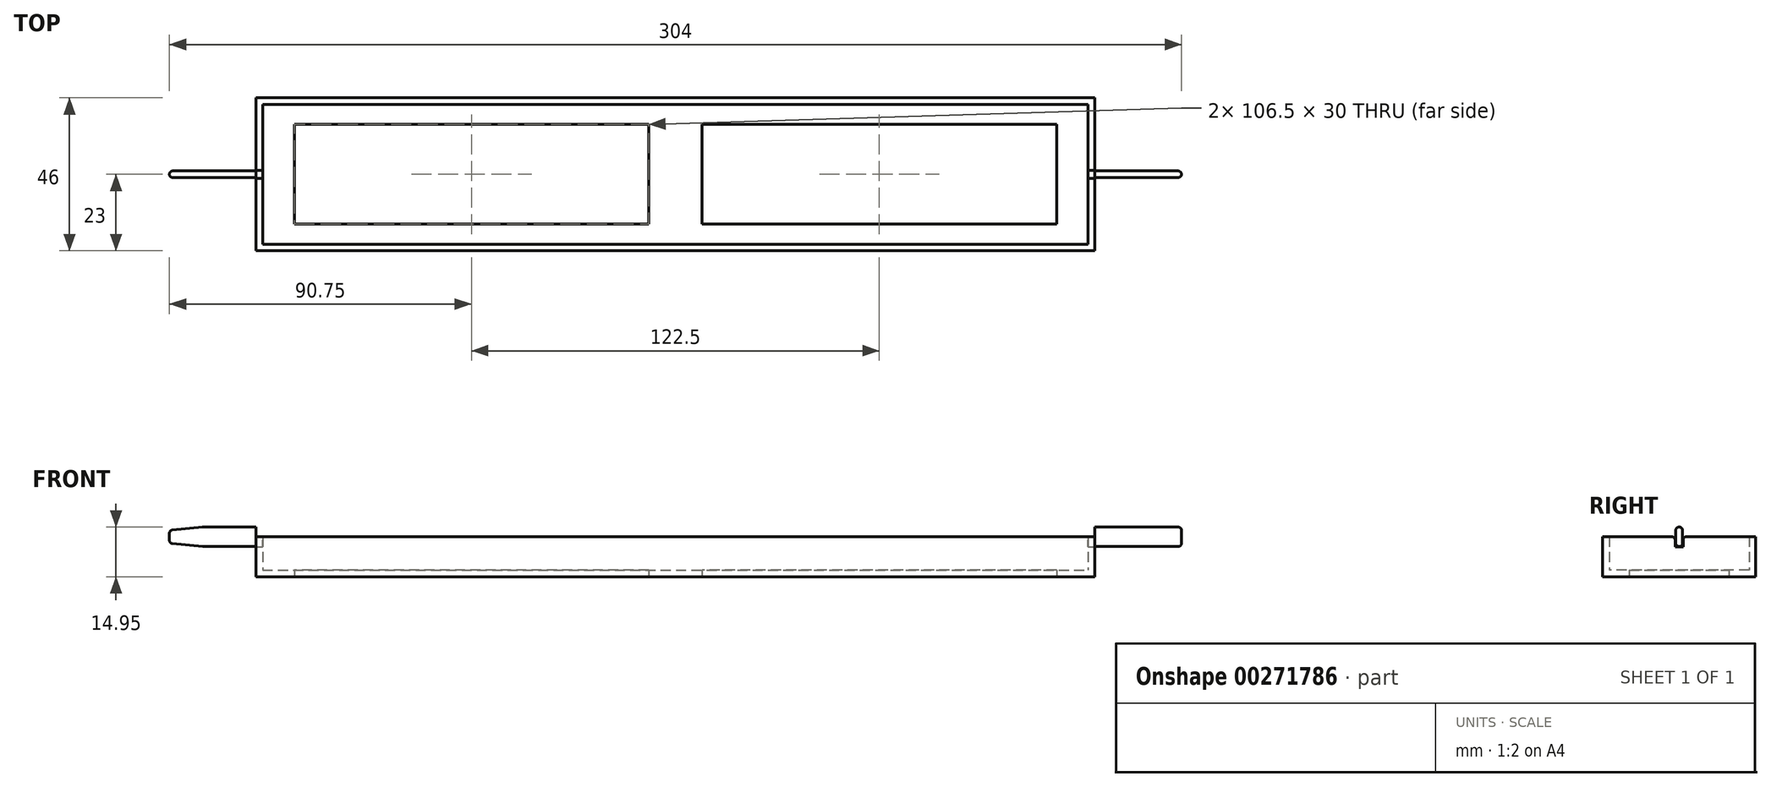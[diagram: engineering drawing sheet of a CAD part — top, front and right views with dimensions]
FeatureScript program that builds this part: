
annotation { "Feature Type Name" : "Feature", "Feature Type Description" : "" }
export const myFeature = defineFeature(function(context is Context, id is Id, definition is map)
    precondition{}
    {
        {
            var Q0;
            Q0=qCreatedBy(makeId("Top.planeOp"),FACE);
            var sketch = newSketch(context, id + "F0", { "sketchPlane" : qUnion([Q0])});
            skLineSegment(sketch, "E0.bottom", {"start": v(126, 23) * mm, "end": v(-126, 23) * mm});
            skLineSegment(sketch, "E0.top", {"start": v(126, -23) * mm, "end": v(-126, -23) * mm});
            skLineSegment(sketch, "E0.left", {"start": v(126, 23) * mm, "end": v(126, -23) * mm});
            skLineSegment(sketch, "E0.right", {"start": v(-126, 23) * mm, "end": v(-126, -23) * mm});
            skPoint(sketch, "E0.middle", {"position": v(0, 0) * mm});
            skLineSegment(sketch, "E1.bottom", {"start": v(114.5, -15) * mm, "end": v(8, -15) * mm});
            skLineSegment(sketch, "E1.top", {"start": v(114.5, 15) * mm, "end": v(8, 15) * mm});
            skLineSegment(sketch, "E1.left", {"start": v(114.5, -15) * mm, "end": v(114.5, 15) * mm});
            skLineSegment(sketch, "E1.right", {"start": v(-114.5, -15) * mm, "end": v(-114.5, 15) * mm});
            skLineSegment(sketch, "E2.left", {"start": v(8, -15) * mm, "end": v(8, 15) * mm});
            skLineSegment(sketch, "E2.right", {"start": v(-8, -15) * mm, "end": v(-8, 15) * mm});
            skLineSegment(sketch, "E3.trimOffspring", {"start": v(-8, 15) * mm, "end": v(-114.5, 15) * mm});
            skLineSegment(sketch, "E4.trimOffspring", {"start": v(-8, -15) * mm, "end": v(-114.5, -15) * mm});
            skSolve(sketch);
        }
        {
            var Q0;
            Q0 = qSketchRegion(id + "F0", true);
            extrude(context, id + "F1", {"entities" : qUnion([Q0]), "depth" : 2 * mm});
        }
        {
            var Q0;
            Q0=makeQuery(id+"F1.opExtrude","CAP_FACE",FACE,{"disambiguationData":[OSD([sQuery(id+"F0.wireOp",EDGE,"E0.bottom"),sQuery(id+"F0.wireOp",EDGE,"E0.top"),sQuery(id+"F0.wireOp",EDGE,"E0.left"),sQuery(id+"F0.wireOp",EDGE,"E0.right")])],"isStart":false});
            var sketch = newSketch(context, id + "F2", { "sketchPlane" : qUnion([Q0])});
            skLineSegment(sketch, "E5.bottom", {"start": v(-126, 23) * mm, "end": v(126, 23) * mm});
            skLineSegment(sketch, "E5.top", {"start": v(-126, -23) * mm, "end": v(126, -23) * mm});
            skLineSegment(sketch, "E5.left", {"start": v(-126, 23) * mm, "end": v(-126, -23) * mm});
            skLineSegment(sketch, "E5.right", {"start": v(126, 23) * mm, "end": v(126, -23) * mm});
            skPoint(sketch, "E5.middle", {"position": v(0, 0) * mm});
            skLineSegment(sketch, "E6.bottom", {"start": v(-124, 21) * mm, "end": v(124, 21) * mm});
            skLineSegment(sketch, "E6.top", {"start": v(-124, -21) * mm, "end": v(124, -21) * mm});
            skLineSegment(sketch, "E6.left", {"start": v(-124, 21) * mm, "end": v(-124, -21) * mm});
            skLineSegment(sketch, "E6.right", {"start": v(124, 21) * mm, "end": v(124, -21) * mm});
            skSolve(sketch);
        }
        {
            var Q0;
            Q0 = qSketchRegion(id + "F2", true);
            extrude(context, id + "F3", {"entities" : qUnion([Q0]), "operationType" : NewBodyOperationType.ADD, "depth" : 10 * mm});
        }
        {
            var Q0;
            Q0=qCreatedBy(makeId("Right.planeOp"),FACE);
            var sketch = newSketch(context, id + "F4", { "sketchPlane" : qUnion([Q0])});
            skLineSegment(sketch, "E7.bottom", {"start": v(-1, 9.05) * mm, "end": v(1, 9.05) * mm});
            skLineSegment(sketch, "E7.top", {"start": v(-1, 14.95) * mm, "end": v(1, 14.95) * mm});
            skLineSegment(sketch, "E7.left", {"start": v(-1, 9.05) * mm, "end": v(-1, 14.95) * mm});
            skLineSegment(sketch, "E7.right", {"start": v(1, 9.05) * mm, "end": v(1, 14.95) * mm});
            skPoint(sketch, "E7.middle", {"position": v(0, 12) * mm});
            skSolve(sketch);
        }
        {
            var Q0;
            Q0 = qSketchRegion(id + "F4", true);
            extrude(context, id + "F5", {"entities" : qUnion([Q0]), "depth" : 152 * mm, "hasSecondDirection" : true, "secondDirectionOppositeDirection" : true, "secondDirectionDepth" : 152 * mm});
        }
        {
            var Q0;
            Q0=makeQuery(id+"F5.opExtrude","CAP_EDGE",EDGE,{"disambiguationData":[OSD([sQuery(id+"F4.wireOp",EDGE,"E7.top")])],"isStart":true});
            var Q1;
            Q1=makeQuery(id+"F5.opExtrude","CAP_EDGE",EDGE,{"disambiguationData":[OSD([sQuery(id+"F4.wireOp",EDGE,"E7.bottom")])],"isStart":true});
            chamfer(context, id + "F6", {"entities" : qUnion([Q0, Q1]), "chamferType" : ChamferType.TWO_OFFSETS, "width1" : 1 * mm, "oppositeDirection" : false, "width2" : 10 * mm, "tangentPropagation" : true});
        }
        {
            var Q0;
            Q0=makeQuery(id+"F5.opExtrude","SWEPT_EDGE",EDGE,{"disambiguationData":[OSD([sQuery(id+"F4.wireOp",EDGE,"E7.top"),sQuery(id+"F4.wireOp",EDGE,"E7.left")])]});
            var Q1;
            Q1=makeQuery(id+"F5.opExtrude","SWEPT_EDGE",EDGE,{"disambiguationData":[OSD([sQuery(id+"F4.wireOp",EDGE,"E7.top"),sQuery(id+"F4.wireOp",EDGE,"E7.right")])]});
            var Q2;
            Q2=makeQuery(id+"F5.opExtrude","SWEPT_EDGE",EDGE,{"disambiguationData":[OSD([sQuery(id+"F4.wireOp",EDGE,"E7.bottom"),sQuery(id+"F4.wireOp",EDGE,"E7.left")])]});
            var Q3;
            Q3=makeQuery(id+"F5.opExtrude","SWEPT_EDGE",EDGE,{"disambiguationData":[OSD([sQuery(id+"F4.wireOp",EDGE,"E7.bottom"),sQuery(id+"F4.wireOp",EDGE,"E7.right")])]});
            var Q4;
            Q4=makeQuery(id+"F5.opExtrude","CAP_FACE",FACE,{"disambiguationData":[OSD([sQuery(id+"F4.wireOp",EDGE,"E7.bottom"),sQuery(id+"F4.wireOp",EDGE,"E7.top"),sQuery(id+"F4.wireOp",EDGE,"E7.left"),sQuery(id+"F4.wireOp",EDGE,"E7.right")])],"isStart":true});
            var Q5;
            Q5=makeQuery(id+"F5.opExtrude","CAP_FACE",FACE,{"disambiguationData":[OSD([sQuery(id+"F4.wireOp",EDGE,"E7.bottom"),sQuery(id+"F4.wireOp",EDGE,"E7.top"),sQuery(id+"F4.wireOp",EDGE,"E7.left"),sQuery(id+"F4.wireOp",EDGE,"E7.right")])],"isStart":false});
            var Q6;
            Q6=makeQuery(id+"F6.opChamfer","BLEND_EDGE",EDGE,{"blendedFrom":[makeQuery(id+"F5.opExtrude","CAP_EDGE",EDGE,{"disambiguationData":[OSD([sQuery(id+"F4.wireOp",EDGE,"E7.top")])],"isStart":true}),makeQuery(id+"F5.opExtrude","SWEPT_FACE",FACE,{"disambiguationData":[OSD([sQuery(id+"F4.wireOp",EDGE,"E7.right")])]})],"blendedInto":[makeQuery(id+"F5.opExtrude","SWEPT_FACE",FACE,{"disambiguationData":[OSD([sQuery(id+"F4.wireOp",EDGE,"E7.right")])]})]});
            var Q7;
            Q7=makeQuery(id+"F6.opChamfer","BLEND_EDGE",EDGE,{"blendedFrom":[makeQuery(id+"F5.opExtrude","CAP_EDGE",EDGE,{"disambiguationData":[OSD([sQuery(id+"F4.wireOp",EDGE,"E7.top")])],"isStart":true}),makeQuery(id+"F5.opExtrude","SWEPT_FACE",FACE,{"disambiguationData":[OSD([sQuery(id+"F4.wireOp",EDGE,"E7.left")])]})],"blendedInto":[makeQuery(id+"F5.opExtrude","SWEPT_FACE",FACE,{"disambiguationData":[OSD([sQuery(id+"F4.wireOp",EDGE,"E7.left")])]})]});
            var Q8;
            Q8=makeQuery(id+"F6.opChamfer","BLEND_EDGE",EDGE,{"blendedFrom":[makeQuery(id+"F5.opExtrude","CAP_EDGE",EDGE,{"disambiguationData":[OSD([sQuery(id+"F4.wireOp",EDGE,"E7.bottom")])],"isStart":true}),makeQuery(id+"F5.opExtrude","SWEPT_FACE",FACE,{"disambiguationData":[OSD([sQuery(id+"F4.wireOp",EDGE,"E7.right")])]})],"blendedInto":[makeQuery(id+"F5.opExtrude","SWEPT_FACE",FACE,{"disambiguationData":[OSD([sQuery(id+"F4.wireOp",EDGE,"E7.right")])]})]});
            var Q9;
            Q9=makeQuery(id+"F6.opChamfer","BLEND_EDGE",EDGE,{"blendedFrom":[makeQuery(id+"F5.opExtrude","CAP_EDGE",EDGE,{"disambiguationData":[OSD([sQuery(id+"F4.wireOp",EDGE,"E7.bottom")])],"isStart":true}),makeQuery(id+"F5.opExtrude","SWEPT_FACE",FACE,{"disambiguationData":[OSD([sQuery(id+"F4.wireOp",EDGE,"E7.left")])]})],"blendedInto":[makeQuery(id+"F5.opExtrude","SWEPT_FACE",FACE,{"disambiguationData":[OSD([sQuery(id+"F4.wireOp",EDGE,"E7.left")])]})]});
            var Q10;
            {var subQ0=sQuery(id+"F4.wireOp",EDGE,"E7.top");Q10=makeQuery(id+"F6.opChamfer","BLEND_EDGE",EDGE,{"blendedFrom":[makeQuery(id+"F5.opExtrude","CAP_EDGE",EDGE,{"disambiguationData":[OSD([subQ0])],"isStart":true}),makeQuery(id+"F5.opExtrude","SWEPT_FACE",FACE,{"disambiguationData":[OSD([subQ0])]})],"blendedInto":[makeQuery(id+"F5.opExtrude","SWEPT_FACE",FACE,{"disambiguationData":[OSD([subQ0])]})]});}
            var Q11;
            {var subQ0=sQuery(id+"F4.wireOp",EDGE,"E7.bottom");Q11=makeQuery(id+"F6.opChamfer","BLEND_EDGE",EDGE,{"blendedFrom":[makeQuery(id+"F5.opExtrude","CAP_EDGE",EDGE,{"disambiguationData":[OSD([subQ0])],"isStart":true}),makeQuery(id+"F5.opExtrude","SWEPT_FACE",FACE,{"disambiguationData":[OSD([subQ0])]})],"blendedInto":[makeQuery(id+"F5.opExtrude","SWEPT_FACE",FACE,{"disambiguationData":[OSD([subQ0])]})]});}
            fillet(context, id + "F7", {"entities" : qUnion([Q0, Q1, Q2, Q3, Q4, Q5, Q6, Q7, Q8, Q9, Q10, Q11]), "radius" : 1 * mm, "tangentPropagation" : true, "allowEdgeOverflow" : false});
        }
        {
            var Q0;
            Q0=qCreatedBy(makeId("Right.planeOp"),FACE);
            var sketch = newSketch(context, id + "F8", { "sketchPlane" : qUnion([Q0])});
            skLineSegment(sketch, "E8.bottom", {"start": v(1.2, 9) * mm, "end": v(-1.2, 9) * mm});
            skLineSegment(sketch, "E8.top", {"start": v(1.2, 15.07) * mm, "end": v(-1.2, 15.07) * mm});
            skLineSegment(sketch, "E8.left", {"start": v(1.2, 9) * mm, "end": v(1.2, 15.07) * mm});
            skLineSegment(sketch, "E8.right", {"start": v(-1.2, 9) * mm, "end": v(-1.2, 15.07) * mm});
            skPoint(sketch, "E8.middle", {"position": v(0, 12.04) * mm});
            skSolve(sketch);
        }
        {
            var Q0;
            Q0 = qSketchRegion(id + "F8", true);
            var Q1;
            Q1=makeQuery(id+"F3.boolean.opBoolean","MERGE",FACE,{"derivedFrom":[makeQuery(id+"F1.opExtrude","SWEPT_FACE",FACE,{"disambiguationData":[OSD([sQuery(id+"F0.wireOp",EDGE,"E0.right")])]}),makeQuery(id+"F3.opExtrude","SWEPT_FACE",FACE,{"disambiguationData":[OSD([sQuery(id+"F2.wireOp",EDGE,"E5.left")])]})]});
            var Q2;
            Q2=makeQuery(id+"F3.boolean.opBoolean","MERGE",FACE,{"derivedFrom":[makeQuery(id+"F1.opExtrude","SWEPT_FACE",FACE,{"disambiguationData":[OSD([sQuery(id+"F0.wireOp",EDGE,"E0.left")])]}),makeQuery(id+"F3.opExtrude","SWEPT_FACE",FACE,{"disambiguationData":[OSD([sQuery(id+"F2.wireOp",EDGE,"E5.right")])]})]});
            extrude(context, id + "F9", {"entities" : qUnion([Q0]), "operationType" : NewBodyOperationType.REMOVE, "endBound" : BoundingType.UP_TO_SURFACE, "oppositeDirection" : true, "endBoundEntityFace" : qUnion([Q1]), "depth" : 125 * mm, "hasSecondDirection" : true, "secondDirectionBound" : SecondDirectionBoundingType.UP_TO_SURFACE, "secondDirectionOppositeDirection" : false, "secondDirectionBoundEntityFace" : qUnion([Q2]), "secondDirectionDepth" : 25 * mm});
        }
        {
            var Q0;
            Q0=makeQuery(id+"F9.boolean.opBoolean","INTERSECT",EDGE,{"disambiguationData":[OD(0.0)],"derivedFrom":[makeQuery(id+"F3.opExtrude","CAP_FACE",FACE,{"disambiguationData":[OSD([sQuery(id+"F2.wireOp",EDGE,"E5.bottom"),sQuery(id+"F2.wireOp",EDGE,"E5.top"),sQuery(id+"F2.wireOp",EDGE,"E5.left"),sQuery(id+"F2.wireOp",EDGE,"E5.right"),sQuery(id+"F2.wireOp",EDGE,"E6.bottom"),sQuery(id+"F2.wireOp",EDGE,"E6.top"),sQuery(id+"F2.wireOp",EDGE,"E6.left"),sQuery(id+"F2.wireOp",EDGE,"E6.right")])],"isStart":false}),makeQuery(id+"F9.opExtrude","SWEPT_FACE",FACE,{"disambiguationData":[OSD([sQuery(id+"F8.wireOp",EDGE,"E8.right")])]})]});
            var Q1;
            Q1=makeQuery(id+"F9.boolean.opBoolean","INTERSECT",EDGE,{"disambiguationData":[OD(0.0)],"derivedFrom":[makeQuery(id+"F3.opExtrude","CAP_FACE",FACE,{"disambiguationData":[OSD([sQuery(id+"F2.wireOp",EDGE,"E5.bottom"),sQuery(id+"F2.wireOp",EDGE,"E5.top"),sQuery(id+"F2.wireOp",EDGE,"E5.left"),sQuery(id+"F2.wireOp",EDGE,"E5.right"),sQuery(id+"F2.wireOp",EDGE,"E6.bottom"),sQuery(id+"F2.wireOp",EDGE,"E6.top"),sQuery(id+"F2.wireOp",EDGE,"E6.left"),sQuery(id+"F2.wireOp",EDGE,"E6.right")])],"isStart":false}),makeQuery(id+"F9.opExtrude","SWEPT_FACE",FACE,{"disambiguationData":[OSD([sQuery(id+"F8.wireOp",EDGE,"E8.left")])]})]});
            var Q2;
            Q2=makeQuery(id+"F9.boolean.opBoolean","INTERSECT",EDGE,{"disambiguationData":[OD(1.0)],"derivedFrom":[makeQuery(id+"F3.opExtrude","CAP_FACE",FACE,{"disambiguationData":[OSD([sQuery(id+"F2.wireOp",EDGE,"E5.bottom"),sQuery(id+"F2.wireOp",EDGE,"E5.top"),sQuery(id+"F2.wireOp",EDGE,"E5.left"),sQuery(id+"F2.wireOp",EDGE,"E5.right"),sQuery(id+"F2.wireOp",EDGE,"E6.bottom"),sQuery(id+"F2.wireOp",EDGE,"E6.top"),sQuery(id+"F2.wireOp",EDGE,"E6.left"),sQuery(id+"F2.wireOp",EDGE,"E6.right")])],"isStart":false}),makeQuery(id+"F9.opExtrude","SWEPT_FACE",FACE,{"disambiguationData":[OSD([sQuery(id+"F8.wireOp",EDGE,"E8.right")])]})]});
            var Q3;
            Q3=makeQuery(id+"F9.boolean.opBoolean","INTERSECT",EDGE,{"disambiguationData":[OD(1.0)],"derivedFrom":[makeQuery(id+"F3.opExtrude","CAP_FACE",FACE,{"disambiguationData":[OSD([sQuery(id+"F2.wireOp",EDGE,"E5.bottom"),sQuery(id+"F2.wireOp",EDGE,"E5.top"),sQuery(id+"F2.wireOp",EDGE,"E5.left"),sQuery(id+"F2.wireOp",EDGE,"E5.right"),sQuery(id+"F2.wireOp",EDGE,"E6.bottom"),sQuery(id+"F2.wireOp",EDGE,"E6.top"),sQuery(id+"F2.wireOp",EDGE,"E6.left"),sQuery(id+"F2.wireOp",EDGE,"E6.right")])],"isStart":false}),makeQuery(id+"F9.opExtrude","SWEPT_FACE",FACE,{"disambiguationData":[OSD([sQuery(id+"F8.wireOp",EDGE,"E8.left")])]})]});
            fillet(context, id + "F10", {"entities" : qUnion([Q0, Q1, Q2, Q3]), "radius" : 1 * mm, "tangentPropagation" : true, "allowEdgeOverflow" : false});
        }
    });
